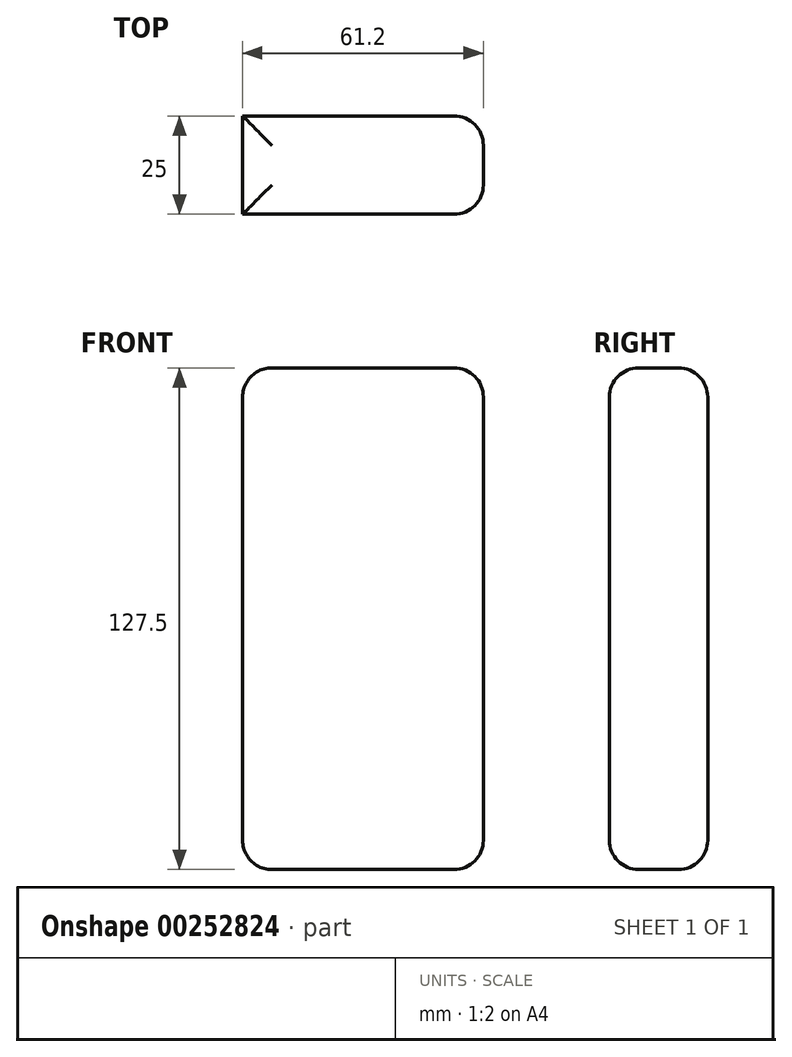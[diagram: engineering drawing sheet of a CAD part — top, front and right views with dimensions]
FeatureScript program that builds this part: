
annotation { "Feature Type Name" : "Feature", "Feature Type Description" : "" }
export const myFeature = defineFeature(function(context is Context, id is Id, definition is map)
    precondition{}
    {
        {
            var Q0;
            Q0=qCreatedBy(makeId("Front.planeOp"),FACE);
            var sketch = newSketch(context, id + "F0", { "sketchPlane" : qUnion([Q0])});
            skLineSegment(sketch, "E0.bottom", {"start": v(30.6, -63.75) * mm, "end": v(-30.6, -63.75) * mm});
            skLineSegment(sketch, "E0.top", {"start": v(30.6, 63.75) * mm, "end": v(-30.6, 63.75) * mm});
            skLineSegment(sketch, "E0.left", {"start": v(30.6, -63.75) * mm, "end": v(30.6, 63.75) * mm});
            skLineSegment(sketch, "E0.right", {"start": v(-30.6, -63.75) * mm, "end": v(-30.6, 63.75) * mm});
            skPoint(sketch, "E0.middle", {"position": v(0, 0) * mm});
            skSolve(sketch);
        }
        {
            var Q0;
            Q0=makeQuery(id+"F0.imprint","IMPRINT",FACE,{"disambiguationData":[TD([[makeQuery(id+"F0.imprint","IMPRINT",EDGE,{"derivedFrom":sQuery(id+"F0.wireOp",EDGE,"E0.bottom")}),-1.0]])]});
            extrude(context, id + "F1", {"entities" : qUnion([Q0]), "endBound" : BoundingType.SYMMETRIC, "depth" : 25 * mm});
        }
        {
            var Q0;
            Q0=makeQuery(id+"F1.opExtrude","SWEPT_EDGE",EDGE,{"disambiguationData":[OSD([sQuery(id+"F0.wireOp",EDGE,"E0.top"),sQuery(id+"F0.wireOp",EDGE,"E0.right")])]});
            var Q1;
            Q1=makeQuery(id+"F1.opExtrude","CAP_EDGE",EDGE,{"disambiguationData":[OSD([sQuery(id+"F0.wireOp",EDGE,"E0.top")])],"isStart":false});
            var Q2;
            Q2=makeQuery(id+"F1.opExtrude","SWEPT_EDGE",EDGE,{"disambiguationData":[OSD([sQuery(id+"F0.wireOp",EDGE,"E0.top"),sQuery(id+"F0.wireOp",EDGE,"E0.left")])]});
            var Q3;
            Q3=makeQuery(id+"F1.opExtrude","CAP_EDGE",EDGE,{"disambiguationData":[OSD([sQuery(id+"F0.wireOp",EDGE,"E0.top")])],"isStart":true});
            var Q4;
            Q4=makeQuery(id+"F1.opExtrude","CAP_EDGE",EDGE,{"disambiguationData":[OSD([sQuery(id+"F0.wireOp",EDGE,"E0.left")])],"isStart":false});
            var Q5;
            Q5=makeQuery(id+"F1.opExtrude","CAP_EDGE",EDGE,{"disambiguationData":[OSD([sQuery(id+"F0.wireOp",EDGE,"E0.left")])],"isStart":true});
            var Q6;
            Q6=makeQuery(id+"F1.opExtrude","CAP_EDGE",EDGE,{"disambiguationData":[OSD([sQuery(id+"F0.wireOp",EDGE,"E0.bottom")])],"isStart":false});
            var Q7;
            Q7=makeQuery(id+"F1.opExtrude","SWEPT_EDGE",EDGE,{"disambiguationData":[OSD([sQuery(id+"F0.wireOp",EDGE,"E0.bottom"),sQuery(id+"F0.wireOp",EDGE,"E0.left")])]});
            var Q8;
            Q8=makeQuery(id+"F1.opExtrude","CAP_EDGE",EDGE,{"disambiguationData":[OSD([sQuery(id+"F0.wireOp",EDGE,"E0.bottom")])],"isStart":true});
            var Q9;
            Q9=makeQuery(id+"F1.opExtrude","SWEPT_EDGE",EDGE,{"disambiguationData":[OSD([sQuery(id+"F0.wireOp",EDGE,"E0.bottom"),sQuery(id+"F0.wireOp",EDGE,"E0.right")])]});
            fillet(context, id + "F2", {"entities" : qUnion([Q0, Q1, Q2, Q3, Q4, Q5, Q6, Q7, Q8, Q9]), "radius" : 7.48 * mm, "tangentPropagation" : true, "allowEdgeOverflow" : false});
        }
    });
